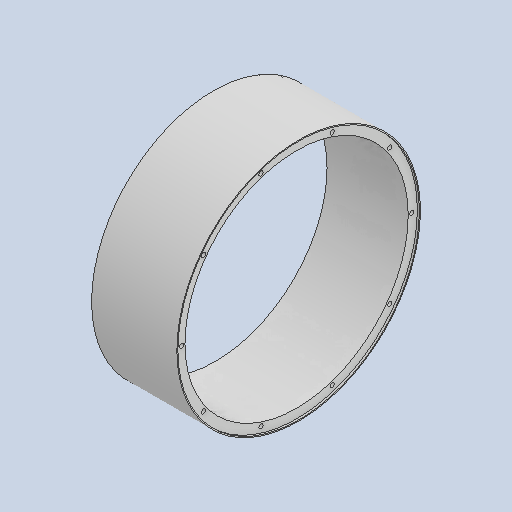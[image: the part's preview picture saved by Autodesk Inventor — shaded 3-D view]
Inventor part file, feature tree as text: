
AUTODESK INVENTOR PART (.ipt)
format: ipt  version: 2024.2 (Build 282272000, 272)  size: 137,216 bytes
history: native  units: in
note: dims shown in document units (in); Inventor stores cm internally (conversion verified against a paired STEP export)
features: mirror x1
ambient origin geometry x8: Origin, YZ Plane, XZ Plane, XY Plane, X Axis, Y Axis, Z Axis, Center Point
bodies: Solid1 (feature_tree)
feature tree (1):
  mirror  "Mirror2"
